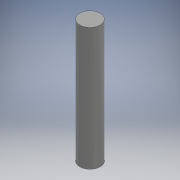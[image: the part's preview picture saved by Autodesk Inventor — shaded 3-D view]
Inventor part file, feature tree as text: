
AUTODESK INVENTOR PART (.ipt)
format: ipt  version: 2018 (Build 220112000, 112)  size: 90,112 bytes
history: native  units: mm
features: extrude x1, sketch x1
ambient origin geometry x8: Origin, YZ Plane, XZ Plane, XY Plane, X Axis, Y Axis, Z Axis, Center Point
bodies: Solid1 (feature_tree)
feature tree (2):
  extrude  "Extrusion1"  Depth=36.0mm TaperAngle=0.0deg
  sketch  "Sketch1"  dims[d0=6.0mm d1=36.0mm d2=0.0mm]
